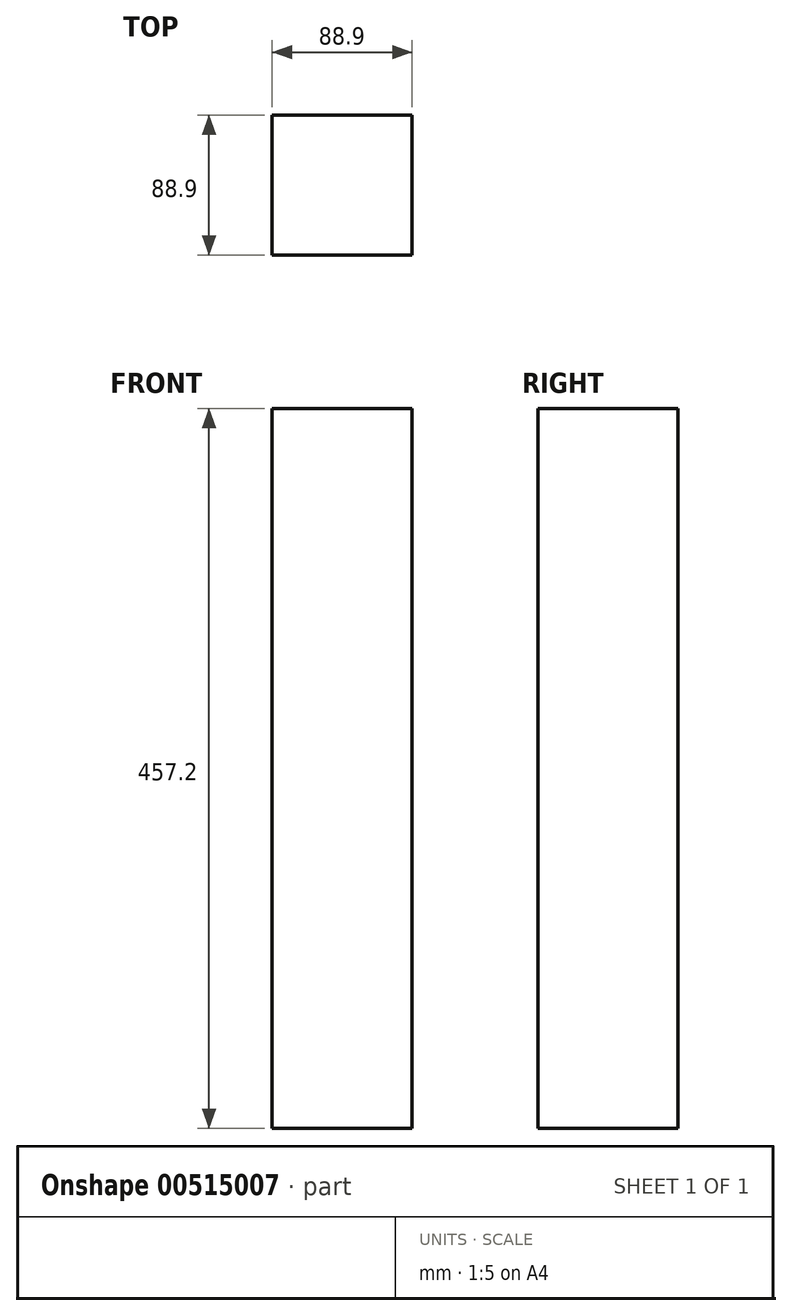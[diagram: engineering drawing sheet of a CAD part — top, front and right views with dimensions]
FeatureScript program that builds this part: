
annotation { "Feature Type Name" : "Feature", "Feature Type Description" : "" }
export const myFeature = defineFeature(function(context is Context, id is Id, definition is map)
    precondition{}
    {
        {
            var Q0;
            Q0=qCreatedBy(makeId("Top.planeOp"),FACE);
            var sketch = newSketch(context, id + "F0", { "sketchPlane" : qUnion([Q0])});
            skLineSegment(sketch, "E0.bottom", {"start": v(-5.32, 0) * mm, "end": v(83.58, 0) * mm});
            skLineSegment(sketch, "E0.top", {"start": v(-5.32, 88.9) * mm, "end": v(83.58, 88.9) * mm});
            skLineSegment(sketch, "E0.left", {"start": v(-5.32, 0) * mm, "end": v(-5.32, 88.9) * mm});
            skLineSegment(sketch, "E0.right", {"start": v(83.58, 0) * mm, "end": v(83.58, 88.9) * mm});
            skSolve(sketch);
        }
        {
            var Q0;
            Q0 = qSketchRegion(id + "F0", true);
            var Q1;
            Q1=makeQuery(id+"F0.imprint","IMPRINT",FACE,{"disambiguationData":[TD([[makeQuery(id+"F0.imprint","IMPRINT",EDGE,{"derivedFrom":sQuery(id+"F0.wireOp",EDGE,"E0.bottom")}),1.0]])]});
            extrude(context, id + "F1", {"entities" : qUnion([Q0, Q1]), "depth" : 457.2 * mm, "offsetDistance" : 25.4 * mm});
        }
    });
